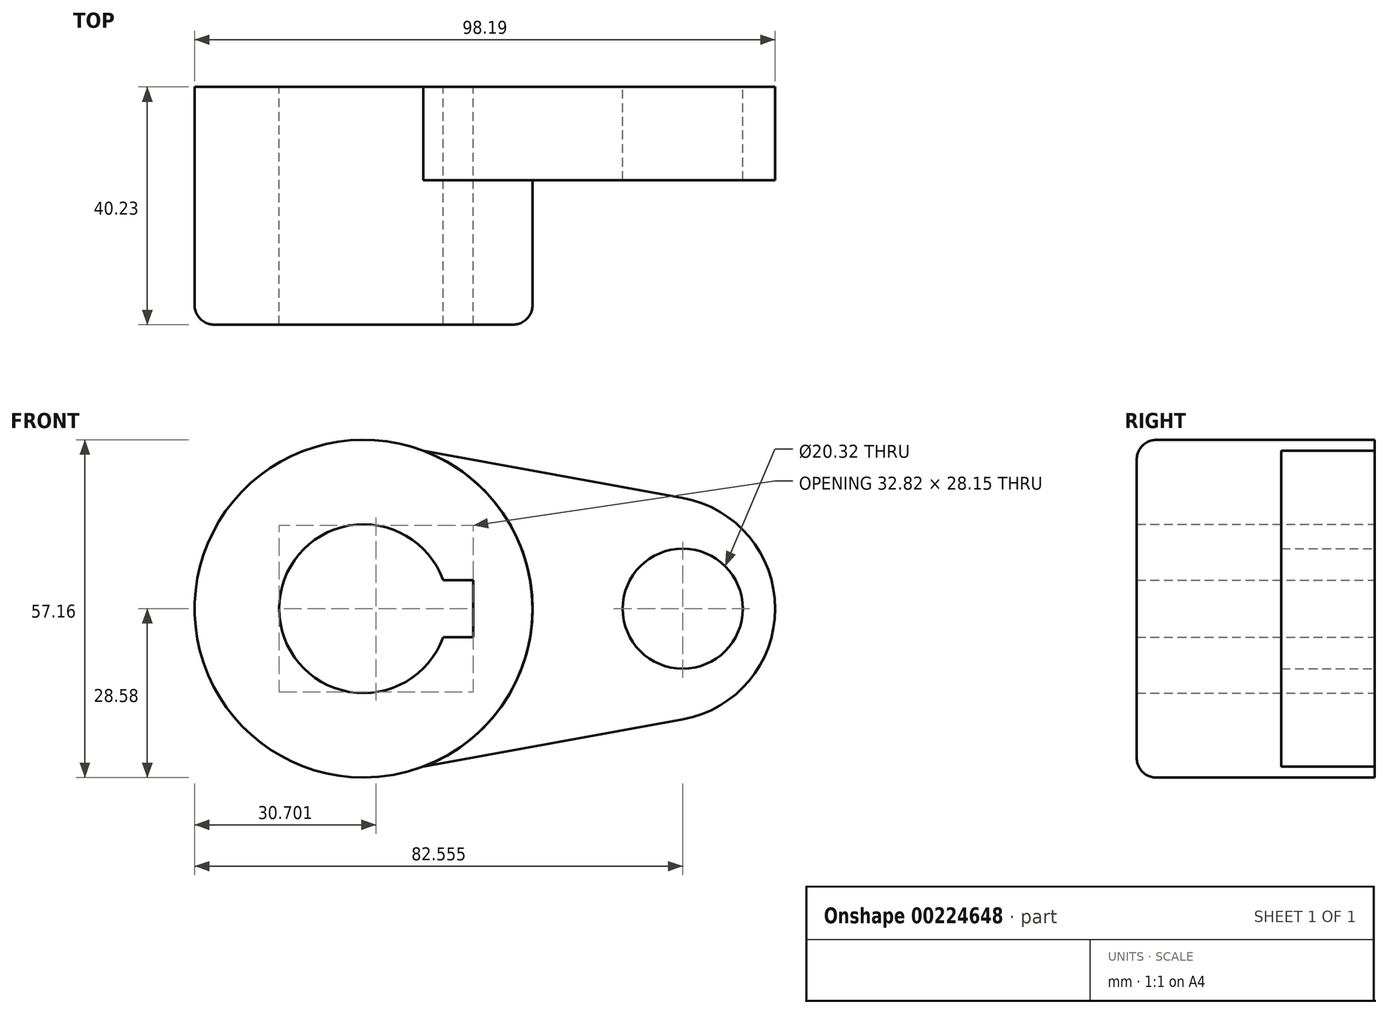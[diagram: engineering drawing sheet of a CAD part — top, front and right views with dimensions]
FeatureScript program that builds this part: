
annotation { "Feature Type Name" : "Feature", "Feature Type Description" : "" }
export const myFeature = defineFeature(function(context is Context, id is Id, definition is map)
    precondition{}
    {
        {
            var Q0;
            Q0=qCreatedBy(makeId("Front.planeOp"),FACE);
            var sketch = newSketch(context, id + "F0", { "sketchPlane" : qUnion([Q0])});
            skCircle(sketch, "E0", {"center": v(0, 0) * mm, "radius": 28.58 * mm});
            skArc(sketch, "E1", {"start": v(13.45, 4.83) * mm, "mid": v(-14.29, 0) * mm, "end": v(13.45, -4.83) * mm});
            skCircle(sketch, "E2", {"center": v(53.98, 0) * mm, "radius": 10.16 * mm});
            skLineSegment(sketch, "E3", {"start": v(10.08, 26.74) * mm, "end": v(53.98, 18.74) * mm});
            skLineSegment(sketch, "E4", {"start": v(10.08, -26.74) * mm, "end": v(53.98, -18.74) * mm});
            skArc(sketch, "E5", {"start": v(53.98, -18.74) * mm, "mid": v(69.61, 0) * mm, "end": v(53.98, 18.74) * mm});
            skLineSegment(sketch, "E6.bottom", {"start": v(18.53, -4.83) * mm, "end": v(13.45, -4.83) * mm});
            skLineSegment(sketch, "E6.top", {"start": v(18.53, 4.83) * mm, "end": v(13.45, 4.83) * mm});
            skLineSegment(sketch, "E6.left", {"start": v(18.53, -4.83) * mm, "end": v(18.53, 4.83) * mm});
            skPoint(sketch, "E7.orphan", {"position": v(0, 28.58) * mm});
            skPoint(sketch, "E8.orphan", {"position": v(0, -28.57) * mm});
            skPoint(sketch, "E9.trimOffspring.end.orphan", {"position": v(-18.53, 4.83) * mm});
            skPoint(sketch, "E10.trimOffspring.end.orphan", {"position": v(-18.53, -4.83) * mm});
            skSolve(sketch);
        }
        {
            var Q0;
            Q0=makeQuery(id+"F0.imprint","IMPRINT",FACE,{"disambiguationData":[TD([[makeQuery(id+"F0.imprint","IMPRINT",EDGE,{"derivedFrom":sQuery(id+"F0.wireOp",EDGE,"E2")}),-1.0]])]});
            extrude(context, id + "F1", {"entities" : qUnion([Q0]), "depth" : 15.77 * mm});
        }
        {
            var Q0;
            Q0=makeQuery(id+"F0.imprint","IMPRINT",FACE,{"disambiguationData":[TD([[makeQuery(id+"F0.imprint","IMPRINT",EDGE,{"derivedFrom":sQuery(id+"F0.wireOp",EDGE,"E1")}),-1.0]])]});
            extrude(context, id + "F2", {"entities" : qUnion([Q0]), "operationType" : NewBodyOperationType.ADD, "depth" : 40.23 * mm});
        }
        {
            var Q0;
            Q0=makeQuery(id+"F2.opExtrude","CAP_EDGE",EDGE,{"disambiguationData":[OSD([sQuery(id+"F0.wireOp",EDGE,"E0")])],"isStart":false});
            fillet(context, id + "F3", {"entities" : qUnion([Q0]), "radius" : 3.3 * mm, "tangentPropagation" : true, "allowEdgeOverflow" : false});
        }
    });
